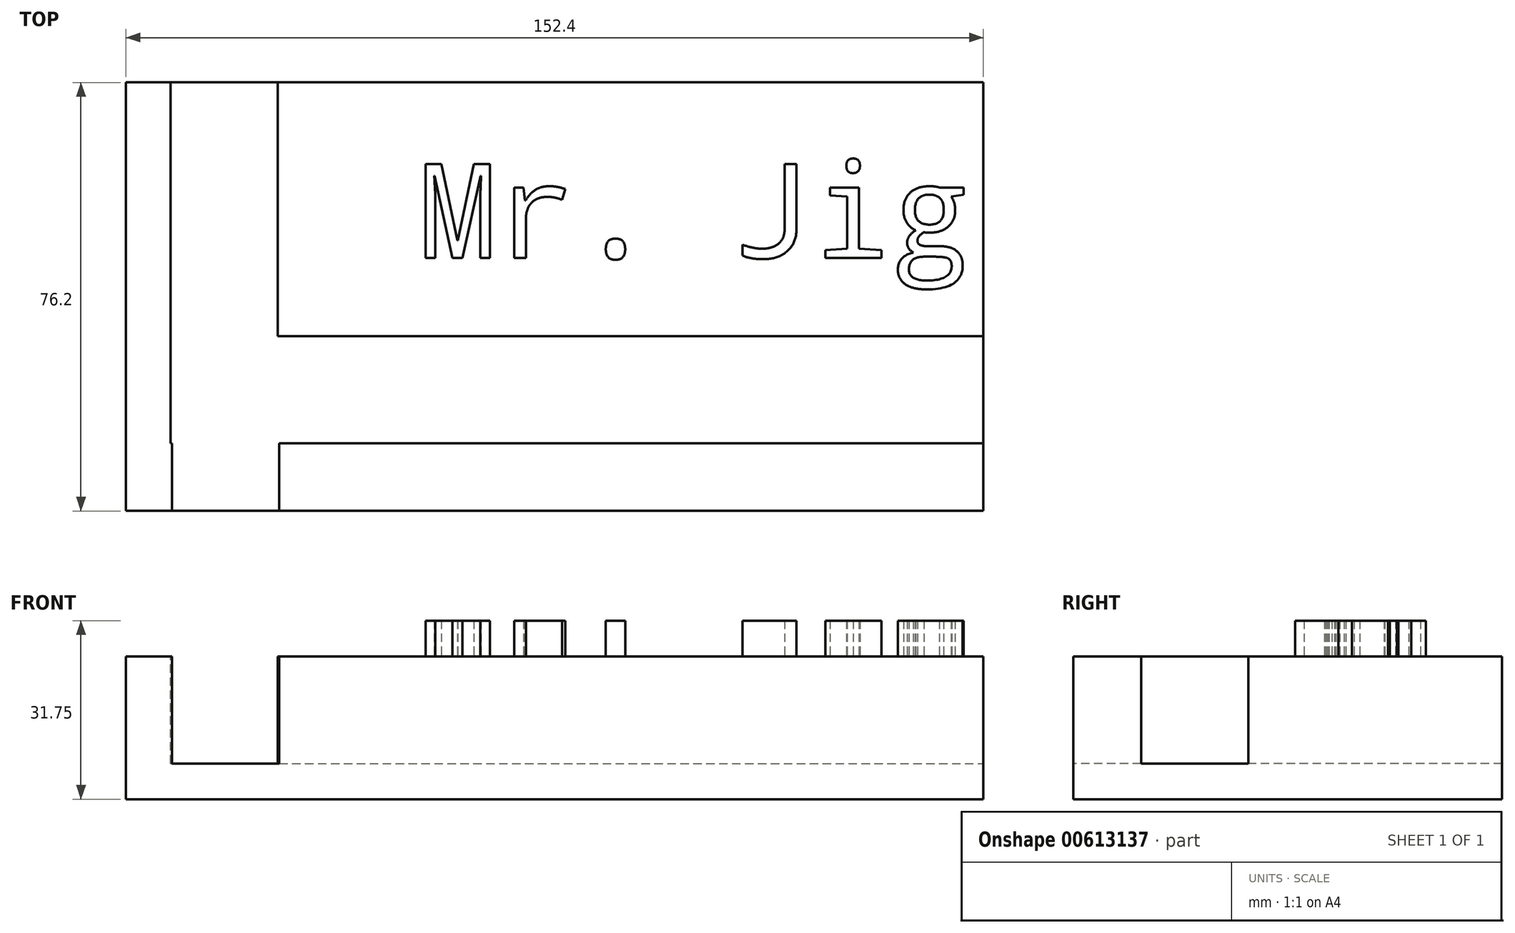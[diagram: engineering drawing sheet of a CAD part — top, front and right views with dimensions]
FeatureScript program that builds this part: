
annotation { "Feature Type Name" : "Feature", "Feature Type Description" : "" }
export const myFeature = defineFeature(function(context is Context, id is Id, definition is map)
    precondition{}
    {
        {
            var Q0;
            Q0=qCreatedBy(makeId("Top.planeOp"),FACE);
            var sketch = newSketch(context, id + "F0", { "sketchPlane" : qUnion([Q0])});
            skLineSegment(sketch, "E0.bottom", {"start": v(-52.12, 31.2) * mm, "end": v(100.28, 31.2) * mm});
            skLineSegment(sketch, "E0.top", {"start": v(-52.12, -45) * mm, "end": v(100.28, -45) * mm});
            skLineSegment(sketch, "E0.left", {"start": v(-52.12, 31.2) * mm, "end": v(-52.12, -45) * mm});
            skLineSegment(sketch, "E0.right", {"start": v(100.28, 31.2) * mm, "end": v(100.28, -45) * mm});
            skSolve(sketch);
        }
        {
            var Q0;
            Q0 = qSketchRegion(id + "F0", true);
            extrude(context, id + "F1", {"entities" : qUnion([Q0]), "depth" : 25.4 * mm, "offsetDistance" : 25.4 * mm});
        }
        {
            var Q0;
            Q0=makeQuery(id+"F1.opExtrude","CAP_FACE",FACE,{"disambiguationData":[OSD([sQuery(id+"F0.wireOp",EDGE,"E0.bottom"),sQuery(id+"F0.wireOp",EDGE,"E0.top"),sQuery(id+"F0.wireOp",EDGE,"E0.left"),sQuery(id+"F0.wireOp",EDGE,"E0.right")])],"isStart":false});
            var sketch = newSketch(context, id + "F2", { "sketchPlane" : qUnion([Q0])});
            skLineSegment(sketch, "E1", {"start": v(-44.23, 31.2) * mm, "end": v(-44.23, -32.95) * mm});
            skLineSegment(sketch, "E2", {"start": v(-44.23, -32.95) * mm, "end": v(100.28, -32.95) * mm});
            skLineSegment(sketch, "E3", {"start": v(100.28, -32.95) * mm, "end": v(100.28, -13.9) * mm});
            skLineSegment(sketch, "E4", {"start": v(100.28, -13.9) * mm, "end": v(-25.18, -13.9) * mm});
            skLineSegment(sketch, "E5", {"start": v(-25.18, -13.9) * mm, "end": v(-25.18, 31.2) * mm});
            skLineSegment(sketch, "E6", {"start": v(-25.18, 31.2) * mm, "end": v(-44.23, 31.2) * mm});
            skSolve(sketch);
        }
        {
            var Q0;
            Q0 = qSketchRegion(id + "F2", true);
            extrude(context, id + "F3", {"entities" : qUnion([Q0]), "operationType" : NewBodyOperationType.REMOVE, "oppositeDirection" : true, "depth" : 19.05 * mm, "offsetDistance" : 25.4 * mm});
        }
        {
            var Q0;
            Q0=makeQuery(id+"F1.opExtrude","SWEPT_FACE",FACE,{"disambiguationData":[OSD([sQuery(id+"F0.wireOp",EDGE,"E0.top")])]});
            var sketch = newSketch(context, id + "F4", { "sketchPlane" : qUnion([Q0])});
            skLineSegment(sketch, "E7.bottom", {"start": v(-43.94, 25.4) * mm, "end": v(-24.89, 25.4) * mm});
            skLineSegment(sketch, "E7.top", {"start": v(-43.94, 6.35) * mm, "end": v(-24.89, 6.35) * mm});
            skLineSegment(sketch, "E7.left", {"start": v(-43.94, 25.4) * mm, "end": v(-43.94, 6.35) * mm});
            skLineSegment(sketch, "E7.right", {"start": v(-24.89, 25.4) * mm, "end": v(-24.89, 6.35) * mm});
            skSolve(sketch);
        }
        {
            var Q0;
            Q0 = qSketchRegion(id + "F4", true);
            extrude(context, id + "F5", {"entities" : qUnion([Q0]), "operationType" : NewBodyOperationType.REMOVE, "oppositeDirection" : true, "depth" : 12.2 * mm, "offsetDistance" : 25.4 * mm});
        }
        {
            var Q0;
            {var subQ0=sQuery(id+"F0.wireOp",EDGE,"E0.bottom");var subQ1=sQuery(id+"F0.wireOp",EDGE,"E0.right");Q0=makeQuery(id+"F3.boolean.opBoolean","SPLIT",FACE,{"disambiguationData":[TD([makeQuery(id+"F3.opExtrude","SWEPT_FACE",FACE,{"disambiguationData":[OSD([sQuery(id+"F2.wireOp",EDGE,"E4")])]})])],"derivedFrom":makeQuery(id+"F1.opExtrude","CAP_FACE",FACE,{"disambiguationData":[OSD([subQ0,sQuery(id+"F0.wireOp",EDGE,"E0.top"),sQuery(id+"F0.wireOp",EDGE,"E0.left"),subQ1])],"isStart":false})});}
            var sketch = newSketch(context, id + "F6", { "sketchPlane" : qUnion([Q0])});
            skText(sketch, "E8", { "text": "Mr. Jig", "fontName": "DroidSansMono.ttf"});
            const initialGuessF6  = {"E8": [-0.00014, 0, 1, 0, 0.01681]};
            skSetInitialGuess(sketch, initialGuessF6);
            skSolve(sketch);
        }
        {
            var Q0;
            Q0 = qSketchRegion(id + "F6", true);
            extrude(context, id + "F7", {"entities" : qUnion([Q0]), "operationType" : NewBodyOperationType.ADD, "depth" : 6.35 * mm, "offsetDistance" : 25.4 * mm});
        }
    });
